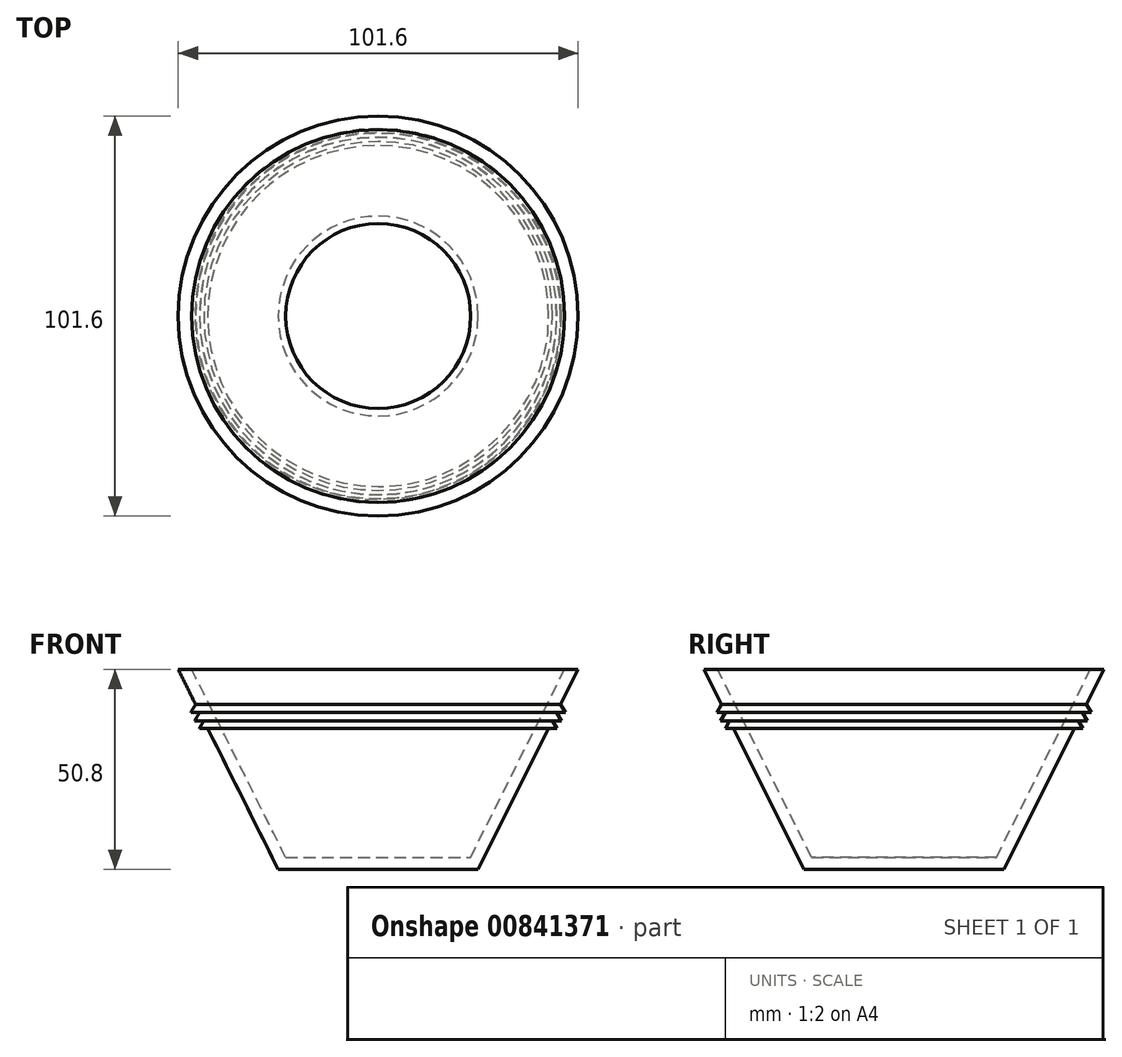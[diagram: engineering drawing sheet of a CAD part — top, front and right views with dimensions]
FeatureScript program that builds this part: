
annotation { "Feature Type Name" : "Feature", "Feature Type Description" : "" }
export const myFeature = defineFeature(function(context is Context, id is Id, definition is map)
    precondition{}
    {
        {
            var Q0;
            Q0=qCreatedBy(makeId("Front.planeOp"),FACE);
            var sketch = newSketch(context, id + "F0", { "sketchPlane" : qUnion([Q0])});
            skLineSegment(sketch, "E0", {"start": v(0, 0) * mm, "end": v(0, 50.8) * mm, "construction": true});
            skLineSegment(sketch, "E1", {"start": v(0, 0) * mm, "end": v(25.4, 0) * mm});
            skLineSegment(sketch, "E2", {"start": v(25.4, 0) * mm, "end": v(50.8, 50.8) * mm});
            skLineSegment(sketch, "E3.0", {"start": v(23.5, 3.07) * mm, "end": v(47.36, 50.8) * mm});
            skLineSegment(sketch, "E3.1", {"start": v(0, 3.07) * mm, "end": v(23.5, 3.07) * mm});
            skLineSegment(sketch, "E4", {"start": v(0, 3.07) * mm, "end": v(0, 0) * mm});
            skLineSegment(sketch, "E5", {"start": v(47.36, 50.8) * mm, "end": v(50.8, 50.8) * mm});
            skLineSegment(sketch, "E6", {"start": v(45.36, 39.92) * mm, "end": v(46.6, 37.78) * mm});
            skLineSegment(sketch, "E7", {"start": v(46.6, 37.78) * mm, "end": v(44.3, 37.78) * mm});
            skLineSegment(sketch, "E8", {"start": v(44.3, 37.78) * mm, "end": v(46.6, 37.78) * mm});
            skLineSegment(sketch, "E9", {"start": v(44.3, 37.78) * mm, "end": v(45.41, 35.83) * mm});
            skLineSegment(sketch, "E10", {"start": v(45.41, 35.83) * mm, "end": v(43.32, 35.83) * mm});
            skLineSegment(sketch, "E11", {"start": v(45.36, 39.92) * mm, "end": v(47.56, 39.92) * mm});
            skLineSegment(sketch, "E12", {"start": v(47.56, 39.92) * mm, "end": v(46.38, 41.96) * mm});
            skSolve(sketch);
        }
        {
            var Q0;
            Q0=makeQuery(id+"F0.imprint","IMPRINT",FACE,{"disambiguationData":[TD([[makeQuery(id+"F0.imprint","IMPRINT",EDGE,{"derivedFrom":sQuery(id+"F0.wireOp",EDGE,"E1")}),1.0]])]});
            var Q1;
            {var subQ0=sQuery(id+"F0.wireOp",EDGE,"E11");Q1=makeQuery(id+"F0.imprint","IMPRINT",FACE,{"disambiguationData":[TD([[makeQuery(id+"F0.imprint","IMPRINT",EDGE,{"derivedFrom":subQ0}),1.0]])]});}
            var Q2;
            {var subQ0=sQuery(id+"F0.wireOp",EDGE,"E6");Q2=makeQuery(id+"F0.imprint","IMPRINT",FACE,{"disambiguationData":[TD([[makeQuery(id+"F0.imprint","IMPRINT",EDGE,{"derivedFrom":subQ0}),-1.0]])]});}
            var Q3;
            {var subQ0=sQuery(id+"F0.wireOp",EDGE,"E9");Q3=makeQuery(id+"F0.imprint","IMPRINT",FACE,{"disambiguationData":[TD([[makeQuery(id+"F0.imprint","IMPRINT",EDGE,{"derivedFrom":subQ0}),-1.0]])]});}
            var Q4;
            Q4=sQuery(id+"F0.wireOp",EDGE,"E0");
            revolve(context, id + "F1", {"surfaceOperationType" : NewSurfaceOperationType.NEW, "entities" : qUnion([Q0, Q1, Q2, Q3]), "axis" : qUnion([Q4]), "revolveType" : RevolveType.FULL});
        }
    });
